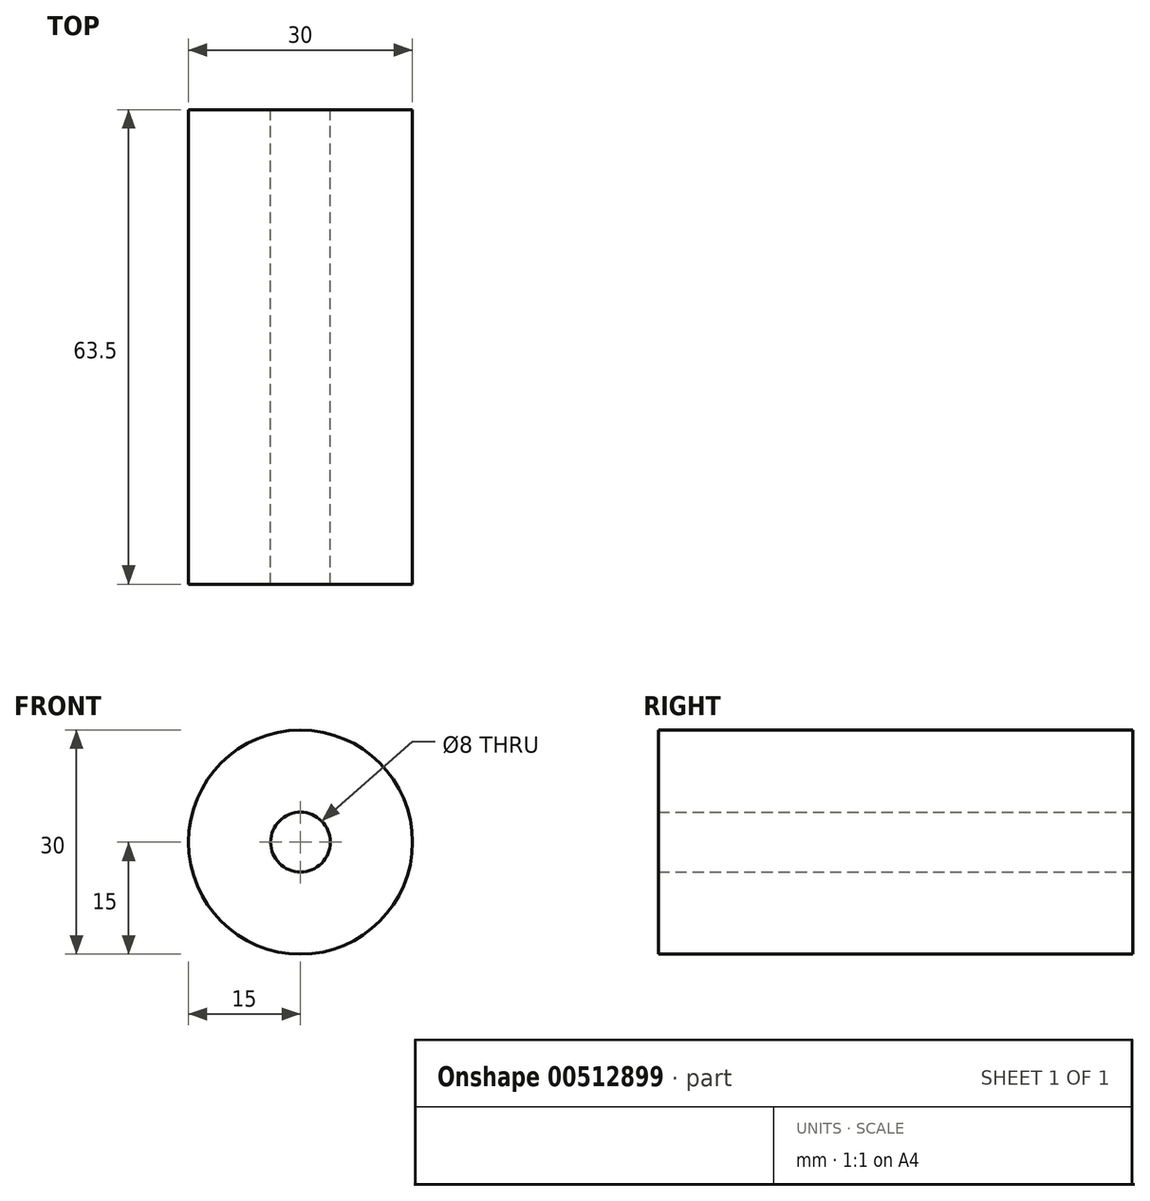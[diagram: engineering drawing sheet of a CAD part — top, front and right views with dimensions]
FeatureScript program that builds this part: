
annotation { "Feature Type Name" : "Feature", "Feature Type Description" : "" }
export const myFeature = defineFeature(function(context is Context, id is Id, definition is map)
    precondition{}
    {
        {
            var Q0;
            Q0=qCreatedBy(makeId("Front.planeOp"),FACE);
            var sketch = newSketch(context, id + "F0", { "sketchPlane" : qUnion([Q0])});
            skCircle(sketch, "E0", {"center": v(0, 0) * mm, "radius": 4 * mm});
            skCircle(sketch, "E1", {"center": v(0, 0) * mm, "radius": 15 * mm});
            skSolve(sketch);
        }
        {
            var Q0;
            Q0 = qSketchRegion(id + "F0", true);
            extrude(context, id + "F1", {"entities" : qUnion([Q0]), "depth" : 254 / 4 * mm, "offsetDistance" : 25 * mm});
        }
    });
